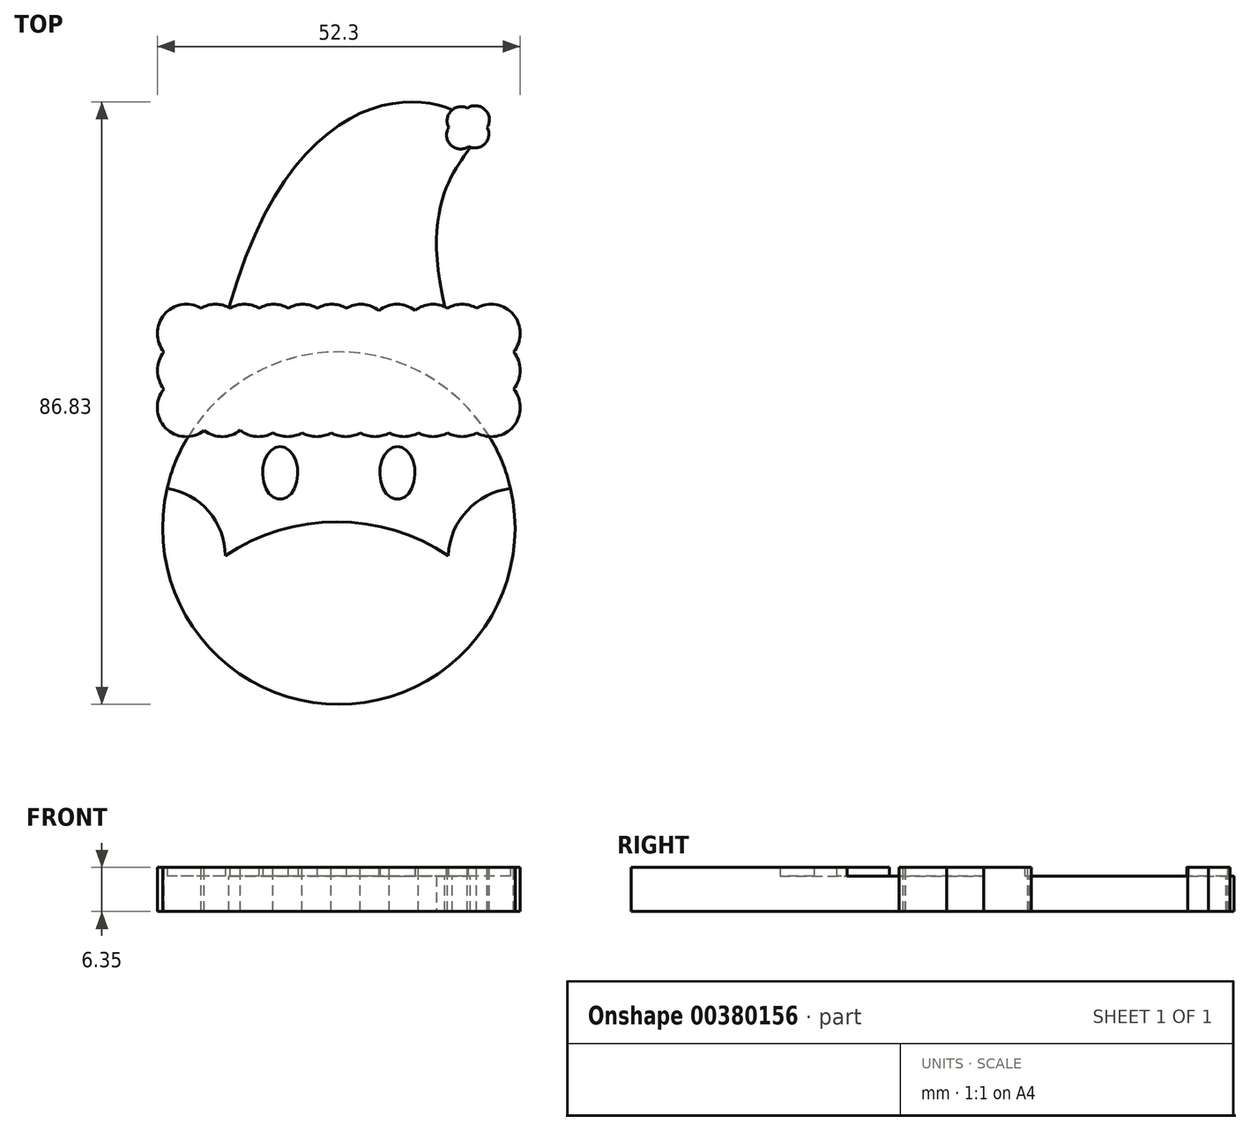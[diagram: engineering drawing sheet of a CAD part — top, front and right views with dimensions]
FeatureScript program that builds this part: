
annotation { "Feature Type Name" : "Feature", "Feature Type Description" : "" }
export const myFeature = defineFeature(function(context is Context, id is Id, definition is map)
    precondition{}
    {
        {
            var Q0;
            Q0=qCreatedBy(makeId("Top.planeOp"),FACE);
            var sketch = newSketch(context, id + "F0", { "sketchPlane" : qUnion([Q0])});
            skCircle(sketch, "E0", {"center": v(0, 0) * mm, "radius": 25.4 * mm});
            skArc(sketch, "E1", {"start": v(-16.36, -3.97) * mm, "mid": v(-18.76, 2.43) * mm, "end": v(-24.75, 5.71) * mm});
            skArc(sketch, "E2", {"start": v(15.78, -3.97) * mm, "mid": v(-0.29, 0.93) * mm, "end": v(-16.36, -3.97) * mm});
            skArc(sketch, "E3", {"start": v(24.75, 5.71) * mm, "mid": v(18.48, 2.52) * mm, "end": v(15.78, -3.97) * mm});
            skSolve(sketch);
        }
        {
            var Q0;
            {var subQ0=sQuery(id+"F0.wireOp",EDGE,"E1");Q0=makeQuery(id+"F0.imprint","IMPRINT",FACE,{"disambiguationData":[TD([[makeQuery(id+"F0.imprint","IMPRINT",EDGE,{"derivedFrom":subQ0}),-1.0]])]});}
            extrude(context, id + "F1", {"entities" : qUnion([Q0]), "depth" : 5.08 * mm});
        }
        {
            var Q0;
            {var subQ0=sQuery(id+"F0.wireOp",EDGE,"E1");Q0=makeQuery(id+"F0.imprint","IMPRINT",FACE,{"disambiguationData":[TD([[makeQuery(id+"F0.imprint","IMPRINT",EDGE,{"derivedFrom":subQ0}),1.0]])]});}
            extrude(context, id + "F2", {"entities" : qUnion([Q0]), "operationType" : NewBodyOperationType.ADD, "depth" : 6.35 * mm});
        }
        {
            var Q0;
            Q0=makeQuery(id+"F1.opExtrude","CAP_FACE",FACE,{"disambiguationData":[OSD([sQuery(id+"F0.wireOp",EDGE,"E0"),sQuery(id+"F0.wireOp",EDGE,"E1"),sQuery(id+"F0.wireOp",EDGE,"E2"),sQuery(id+"F0.wireOp",EDGE,"E3")])],"isStart":false});
            var sketch = newSketch(context, id + "F3", { "sketchPlane" : qUnion([Q0])});
            skLineSegment(sketch, "E4.bottom", {"start": v(21.96, 28.07) * mm, "end": v(-21.96, 28.07) * mm, "construction": true});
            skLineSegment(sketch, "E4.top", {"start": v(21.96, 17.38) * mm, "end": v(-21.96, 17.38) * mm, "construction": true});
            skLineSegment(sketch, "E4.left", {"start": v(21.96, 28.07) * mm, "end": v(21.96, 17.38) * mm, "construction": true});
            skLineSegment(sketch, "E4.right", {"start": v(-21.96, 28.07) * mm, "end": v(-21.96, 17.38) * mm, "construction": true});
            skPoint(sketch, "E4.middle", {"position": v(0, 22.72) * mm});
            skCircle(sketch, "E5", {"center": v(-21.96, 28.07) * mm, "radius": 4.2 * mm});
            skCircle(sketch, "E6", {"center": v(-21.96, 22.72) * mm, "radius": 4.2 * mm});
            skCircle(sketch, "E7", {"center": v(-21.96, 17.38) * mm, "radius": 4.2 * mm});
            skCircle(sketch, "E8", {"center": v(-17.77, 28.07) * mm, "radius": 4.2 * mm});
            skCircle(sketch, "E9", {"center": v(-13.58, 28.07) * mm, "radius": 4.2 * mm});
            skCircle(sketch, "E10", {"center": v(-9.39, 28.07) * mm, "radius": 4.2 * mm});
            skCircle(sketch, "E11", {"center": v(-5.2, 28.07) * mm, "radius": 4.2 * mm});
            skPoint(sketch, "E11.centerSnap0", {"position": v(0, 28.07) * mm});
            skCircle(sketch, "E12", {"center": v(-1, 28.07) * mm, "radius": 4.2 * mm});
            skCircle(sketch, "E13", {"center": v(3.19, 28.07) * mm, "radius": 4.2 * mm});
            skCircle(sketch, "E14", {"center": v(21.96, 28.07) * mm, "radius": 4.2 * mm});
            skCircle(sketch, "E15", {"center": v(17.77, 28.07) * mm, "radius": 4.2 * mm});
            skCircle(sketch, "E16", {"center": v(13.58, 28.07) * mm, "radius": 4.2 * mm});
            skCircle(sketch, "E17", {"center": v(8.4, 28.07) * mm, "radius": 4.2 * mm});
            skCircle(sketch, "E18", {"center": v(21.96, 22.72) * mm, "radius": 4.2 * mm});
            skCircle(sketch, "E19", {"center": v(21.96, 17.38) * mm, "radius": 4.2 * mm});
            skCircle(sketch, "E20", {"center": v(17.77, 17.38) * mm, "radius": 4.2 * mm});
            skCircle(sketch, "E21", {"center": v(13.58, 17.38) * mm, "radius": 4.2 * mm});
            skCircle(sketch, "E22", {"center": v(9.39, 17.38) * mm, "radius": 4.2 * mm});
            skCircle(sketch, "E23", {"center": v(5.2, 17.38) * mm, "radius": 4.2 * mm});
            skCircle(sketch, "E24", {"center": v(1, 17.38) * mm, "radius": 4.2 * mm});
            skCircle(sketch, "E25", {"center": v(-3.19, 17.38) * mm, "radius": 4.2 * mm});
            skCircle(sketch, "E26", {"center": v(-7.38, 17.38) * mm, "radius": 4.2 * mm});
            skCircle(sketch, "E27", {"center": v(-11.57, 17.38) * mm, "radius": 4.2 * mm});
            skCircle(sketch, "E28", {"center": v(-16.84, 17.38) * mm, "radius": 4.2 * mm});
            skSolve(sketch);
        }
        {
            var Q0;
            {var subQ0=sQuery(id+"F3.wireOp",EDGE,"E8");var subQ1=sQuery(id+"F3.wireOp",EDGE,"E5");var subQ2=makeQuery(id+"F3.imprint","INTERSECT",VERTEX,{"disambiguationData":[OD(0.0)],"derivedFrom":[subQ1,subQ0]});Q0=makeQuery(id+"F3.imprint","IMPRINT",FACE,{"disambiguationData":[TD([[makeQuery(id+"F3.imprint","IMPRINT",EDGE,{"disambiguationData":[TD([[subQ2,-1.0]])],"derivedFrom":subQ1}),1.0]])]});}
            var Q1;
            {var subQ0=sQuery(id+"F3.wireOp",EDGE,"E8");var subQ1=sQuery(id+"F3.wireOp",EDGE,"E5");var subQ2=makeQuery(id+"F3.imprint","INTERSECT",VERTEX,{"disambiguationData":[OD(0.0)],"derivedFrom":[subQ1,subQ0]});Q1=makeQuery(id+"F3.imprint","IMPRINT",FACE,{"disambiguationData":[TD([[makeQuery(id+"F3.imprint","IMPRINT",EDGE,{"disambiguationData":[TD([[subQ2,1.0]])],"derivedFrom":subQ1}),1.0]])]});}
            var Q2;
            {var subQ0=sQuery(id+"F3.wireOp",EDGE,"E8");var subQ1=sQuery(id+"F3.wireOp",EDGE,"E5");var subQ2=makeQuery(id+"F3.imprint","INTERSECT",VERTEX,{"disambiguationData":[OD(0.0)],"derivedFrom":[subQ1,subQ0]});Q2=makeQuery(id+"F3.imprint","IMPRINT",FACE,{"disambiguationData":[TD([[makeQuery(id+"F3.imprint","IMPRINT",EDGE,{"disambiguationData":[TD([[subQ2,1.0]])],"derivedFrom":subQ1}),-1.0]])]});}
            var Q3;
            {var subQ0=sQuery(id+"F3.wireOp",EDGE,"E9");var subQ1=sQuery(id+"F3.wireOp",EDGE,"E8");var subQ2=makeQuery(id+"F3.imprint","INTERSECT",VERTEX,{"disambiguationData":[OD(0.0)],"derivedFrom":[subQ1,subQ0]});Q3=makeQuery(id+"F3.imprint","IMPRINT",FACE,{"disambiguationData":[TD([[makeQuery(id+"F3.imprint","IMPRINT",EDGE,{"disambiguationData":[TD([[subQ2,1.0]])],"derivedFrom":subQ1}),1.0]])]});}
            var Q4;
            {var subQ0=sQuery(id+"F3.wireOp",EDGE,"E9");var subQ1=sQuery(id+"F3.wireOp",EDGE,"E5");var subQ2=makeQuery(id+"F3.imprint","INTERSECT",VERTEX,{"derivedFrom":[subQ1,subQ0]});Q4=makeQuery(id+"F3.imprint","IMPRINT",FACE,{"disambiguationData":[TD([[makeQuery(id+"F3.imprint","IMPRINT",EDGE,{"disambiguationData":[TD([[subQ2,1.0]])],"derivedFrom":subQ1}),-1.0]])]});}
            var Q5;
            {var subQ5=sQuery(id+"F3.wireOp",EDGE,"E8");var subQ7=sQuery(id+"F3.wireOp",EDGE,"E6");var subQ8=makeQuery(id+"F3.imprint","INTERSECT",VERTEX,{"disambiguationData":[OD(0.0)],"derivedFrom":[subQ7,subQ5]});Q5=makeQuery(id+"F3.imprint","IMPRINT",FACE,{"disambiguationData":[TD([[makeQuery(id+"F3.imprint","IMPRINT",EDGE,{"disambiguationData":[TD([[subQ8,1.0]])],"derivedFrom":subQ7}),-1.0]])]});}
            var Q6;
            {var subQ1=sQuery(id+"F3.wireOp",EDGE,"E15");var subQ5=sQuery(id+"F3.wireOp",EDGE,"E16");var subQ6=makeQuery(id+"F3.imprint","INTERSECT",VERTEX,{"disambiguationData":[OD(1.0)],"derivedFrom":[subQ1,subQ5]});Q6=makeQuery(id+"F3.imprint","IMPRINT",FACE,{"disambiguationData":[TD([[makeQuery(id+"F3.imprint","IMPRINT",EDGE,{"disambiguationData":[TD([[subQ6,-1.0]])],"derivedFrom":subQ1}),-1.0]])]});}
            var Q7;
            {var subQ0=sQuery(id+"F3.wireOp",EDGE,"E10");var subQ1=sQuery(id+"F3.wireOp",EDGE,"E8");var subQ2=makeQuery(id+"F3.imprint","INTERSECT",VERTEX,{"derivedFrom":[subQ1,subQ0]});Q7=makeQuery(id+"F3.imprint","IMPRINT",FACE,{"disambiguationData":[TD([[makeQuery(id+"F3.imprint","IMPRINT",EDGE,{"disambiguationData":[TD([[subQ2,1.0]])],"derivedFrom":subQ1}),-1.0]])]});}
            var Q8;
            {var subQ0=sQuery(id+"F3.wireOp",EDGE,"E9");var subQ1=sQuery(id+"F3.wireOp",EDGE,"E8");var subQ2=makeQuery(id+"F3.imprint","INTERSECT",VERTEX,{"disambiguationData":[OD(0.0)],"derivedFrom":[subQ1,subQ0]});Q8=makeQuery(id+"F3.imprint","IMPRINT",FACE,{"disambiguationData":[TD([[makeQuery(id+"F3.imprint","IMPRINT",EDGE,{"disambiguationData":[TD([[subQ2,1.0]])],"derivedFrom":subQ1}),-1.0]])]});}
            var Q9;
            {var subQ0=sQuery(id+"F3.wireOp",EDGE,"E10");var subQ1=sQuery(id+"F3.wireOp",EDGE,"E9");var subQ2=makeQuery(id+"F3.imprint","INTERSECT",VERTEX,{"disambiguationData":[OD(0.0)],"derivedFrom":[subQ1,subQ0]});Q9=makeQuery(id+"F3.imprint","IMPRINT",FACE,{"disambiguationData":[TD([[makeQuery(id+"F3.imprint","IMPRINT",EDGE,{"disambiguationData":[TD([[subQ2,1.0]])],"derivedFrom":subQ1}),1.0]])]});}
            var Q10;
            {var subQ0=sQuery(id+"F3.wireOp",EDGE,"E10");var subQ1=sQuery(id+"F3.wireOp",EDGE,"E9");var subQ2=makeQuery(id+"F3.imprint","INTERSECT",VERTEX,{"disambiguationData":[OD(0.0)],"derivedFrom":[subQ1,subQ0]});Q10=makeQuery(id+"F3.imprint","IMPRINT",FACE,{"disambiguationData":[TD([[makeQuery(id+"F3.imprint","IMPRINT",EDGE,{"disambiguationData":[TD([[subQ2,1.0]])],"derivedFrom":subQ1}),-1.0]])]});}
            var Q11;
            {var subQ0=sQuery(id+"F3.wireOp",EDGE,"E11");var subQ1=sQuery(id+"F3.wireOp",EDGE,"E10");var subQ2=makeQuery(id+"F3.imprint","INTERSECT",VERTEX,{"disambiguationData":[OD(0.0)],"derivedFrom":[subQ1,subQ0]});Q11=makeQuery(id+"F3.imprint","IMPRINT",FACE,{"disambiguationData":[TD([[makeQuery(id+"F3.imprint","IMPRINT",EDGE,{"disambiguationData":[TD([[subQ2,1.0]])],"derivedFrom":subQ1}),1.0]])]});}
            var Q12;
            {var subQ0=sQuery(id+"F3.wireOp",EDGE,"E11");var subQ1=sQuery(id+"F3.wireOp",EDGE,"E10");var subQ2=makeQuery(id+"F3.imprint","INTERSECT",VERTEX,{"disambiguationData":[OD(0.0)],"derivedFrom":[subQ1,subQ0]});Q12=makeQuery(id+"F3.imprint","IMPRINT",FACE,{"disambiguationData":[TD([[makeQuery(id+"F3.imprint","IMPRINT",EDGE,{"disambiguationData":[TD([[subQ2,1.0]])],"derivedFrom":subQ1}),1.0]])]});}
            var Q13;
            {var subQ0=sQuery(id+"F3.wireOp",EDGE,"E11");var subQ1=sQuery(id+"F3.wireOp",EDGE,"E9");var subQ2=makeQuery(id+"F3.imprint","INTERSECT",VERTEX,{"derivedFrom":[subQ1,subQ0]});Q13=makeQuery(id+"F3.imprint","IMPRINT",FACE,{"disambiguationData":[TD([[makeQuery(id+"F3.imprint","IMPRINT",EDGE,{"disambiguationData":[TD([[subQ2,1.0]])],"derivedFrom":subQ1}),-1.0]])]});}
            var Q14;
            {var subQ0=sQuery(id+"F3.wireOp",EDGE,"E12");var subQ1=sQuery(id+"F3.wireOp",EDGE,"E10");var subQ2=makeQuery(id+"F3.imprint","INTERSECT",VERTEX,{"derivedFrom":[subQ1,subQ0]});Q14=makeQuery(id+"F3.imprint","IMPRINT",FACE,{"disambiguationData":[TD([[makeQuery(id+"F3.imprint","IMPRINT",EDGE,{"disambiguationData":[TD([[subQ2,1.0]])],"derivedFrom":subQ1}),-1.0]])]});}
            var Q15;
            {var subQ0=sQuery(id+"F3.wireOp",EDGE,"E12");var subQ1=sQuery(id+"F3.wireOp",EDGE,"E11");var subQ2=makeQuery(id+"F3.imprint","INTERSECT",VERTEX,{"disambiguationData":[OD(0.0)],"derivedFrom":[subQ1,subQ0]});Q15=makeQuery(id+"F3.imprint","IMPRINT",FACE,{"disambiguationData":[TD([[makeQuery(id+"F3.imprint","IMPRINT",EDGE,{"disambiguationData":[TD([[subQ2,1.0]])],"derivedFrom":subQ1}),1.0]])]});}
            var Q16;
            {var subQ0=sQuery(id+"F3.wireOp",EDGE,"E11");var subQ1=sQuery(id+"F3.wireOp",EDGE,"E10");var subQ2=makeQuery(id+"F3.imprint","INTERSECT",VERTEX,{"disambiguationData":[OD(0.0)],"derivedFrom":[subQ1,subQ0]});Q16=makeQuery(id+"F3.imprint","IMPRINT",FACE,{"disambiguationData":[TD([[makeQuery(id+"F3.imprint","IMPRINT",EDGE,{"disambiguationData":[TD([[subQ2,1.0]])],"derivedFrom":subQ1}),-1.0]])]});}
            var Q17;
            {var subQ0=sQuery(id+"F3.wireOp",EDGE,"E13");var subQ1=sQuery(id+"F3.wireOp",EDGE,"E11");var subQ2=makeQuery(id+"F3.imprint","INTERSECT",VERTEX,{"derivedFrom":[subQ1,subQ0]});Q17=makeQuery(id+"F3.imprint","IMPRINT",FACE,{"disambiguationData":[TD([[makeQuery(id+"F3.imprint","IMPRINT",EDGE,{"disambiguationData":[TD([[subQ2,1.0]])],"derivedFrom":subQ1}),-1.0]])]});}
            var Q18;
            {var subQ0=sQuery(id+"F3.wireOp",EDGE,"E13");var subQ1=sQuery(id+"F3.wireOp",EDGE,"E12");var subQ2=makeQuery(id+"F3.imprint","INTERSECT",VERTEX,{"disambiguationData":[OD(0.0)],"derivedFrom":[subQ1,subQ0]});Q18=makeQuery(id+"F3.imprint","IMPRINT",FACE,{"disambiguationData":[TD([[makeQuery(id+"F3.imprint","IMPRINT",EDGE,{"disambiguationData":[TD([[subQ2,1.0]])],"derivedFrom":subQ1}),1.0]])]});}
            var Q19;
            {var subQ0=sQuery(id+"F3.wireOp",EDGE,"E12");var subQ1=sQuery(id+"F3.wireOp",EDGE,"E11");var subQ2=makeQuery(id+"F3.imprint","INTERSECT",VERTEX,{"disambiguationData":[OD(0.0)],"derivedFrom":[subQ1,subQ0]});Q19=makeQuery(id+"F3.imprint","IMPRINT",FACE,{"disambiguationData":[TD([[makeQuery(id+"F3.imprint","IMPRINT",EDGE,{"disambiguationData":[TD([[subQ2,1.0]])],"derivedFrom":subQ1}),-1.0]])]});}
            var Q20;
            {var subQ1=sQuery(id+"F3.wireOp",EDGE,"E13");var subQ5=sQuery(id+"F3.wireOp",EDGE,"E12");var subQ6=makeQuery(id+"F3.imprint","INTERSECT",VERTEX,{"disambiguationData":[OD(0.0)],"derivedFrom":[subQ5,subQ1]});Q20=makeQuery(id+"F3.imprint","IMPRINT",FACE,{"disambiguationData":[TD([[makeQuery(id+"F3.imprint","IMPRINT",EDGE,{"disambiguationData":[TD([[subQ6,1.0]])],"derivedFrom":subQ5}),-1.0]])]});}
            var Q21;
            {var subQ0=sQuery(id+"F3.wireOp",EDGE,"E17");var subQ1=sQuery(id+"F3.wireOp",EDGE,"E13");var subQ2=makeQuery(id+"F3.imprint","INTERSECT",VERTEX,{"disambiguationData":[OD(0.0)],"derivedFrom":[subQ1,subQ0]});Q21=makeQuery(id+"F3.imprint","IMPRINT",FACE,{"disambiguationData":[TD([[makeQuery(id+"F3.imprint","IMPRINT",EDGE,{"disambiguationData":[TD([[subQ2,1.0]])],"derivedFrom":subQ1}),1.0]])]});}
            var Q22;
            {var subQ0=sQuery(id+"F3.wireOp",EDGE,"E17");var subQ1=sQuery(id+"F3.wireOp",EDGE,"E13");var subQ2=makeQuery(id+"F3.imprint","INTERSECT",VERTEX,{"disambiguationData":[OD(0.0)],"derivedFrom":[subQ1,subQ0]});Q22=makeQuery(id+"F3.imprint","IMPRINT",FACE,{"disambiguationData":[TD([[makeQuery(id+"F3.imprint","IMPRINT",EDGE,{"disambiguationData":[TD([[subQ2,1.0]])],"derivedFrom":subQ1}),-1.0]])]});}
            var Q23;
            {var subQ0=sQuery(id+"F3.wireOp",EDGE,"E17");var subQ1=sQuery(id+"F3.wireOp",EDGE,"E16");var subQ2=makeQuery(id+"F3.imprint","INTERSECT",VERTEX,{"disambiguationData":[OD(0.0)],"derivedFrom":[subQ1,subQ0]});Q23=makeQuery(id+"F3.imprint","IMPRINT",FACE,{"disambiguationData":[TD([[makeQuery(id+"F3.imprint","IMPRINT",EDGE,{"disambiguationData":[TD([[subQ2,-1.0]])],"derivedFrom":subQ1}),1.0]])]});}
            var Q24;
            {var subQ0=sQuery(id+"F3.wireOp",EDGE,"E16");var subQ1=sQuery(id+"F3.wireOp",EDGE,"E15");var subQ2=makeQuery(id+"F3.imprint","INTERSECT",VERTEX,{"disambiguationData":[OD(0.0)],"derivedFrom":[subQ1,subQ0]});Q24=makeQuery(id+"F3.imprint","IMPRINT",FACE,{"disambiguationData":[TD([[makeQuery(id+"F3.imprint","IMPRINT",EDGE,{"disambiguationData":[TD([[subQ2,-1.0]])],"derivedFrom":subQ1}),-1.0]])]});}
            var Q25;
            {var subQ0=sQuery(id+"F3.wireOp",EDGE,"E16");var subQ1=sQuery(id+"F3.wireOp",EDGE,"E15");var subQ2=makeQuery(id+"F3.imprint","INTERSECT",VERTEX,{"disambiguationData":[OD(0.0)],"derivedFrom":[subQ1,subQ0]});Q25=makeQuery(id+"F3.imprint","IMPRINT",FACE,{"disambiguationData":[TD([[makeQuery(id+"F3.imprint","IMPRINT",EDGE,{"disambiguationData":[TD([[subQ2,-1.0]])],"derivedFrom":subQ1}),1.0]])]});}
            var Q26;
            {var subQ0=sQuery(id+"F3.wireOp",EDGE,"E15");var subQ1=sQuery(id+"F3.wireOp",EDGE,"E14");var subQ2=makeQuery(id+"F3.imprint","INTERSECT",VERTEX,{"disambiguationData":[OD(0.0)],"derivedFrom":[subQ1,subQ0]});Q26=makeQuery(id+"F3.imprint","IMPRINT",FACE,{"disambiguationData":[TD([[makeQuery(id+"F3.imprint","IMPRINT",EDGE,{"disambiguationData":[TD([[subQ2,-1.0]])],"derivedFrom":subQ1}),-1.0]])]});}
            var Q27;
            {var subQ0=sQuery(id+"F3.wireOp",EDGE,"E16");var subQ1=sQuery(id+"F3.wireOp",EDGE,"E14");var subQ2=makeQuery(id+"F3.imprint","INTERSECT",VERTEX,{"derivedFrom":[subQ1,subQ0]});Q27=makeQuery(id+"F3.imprint","IMPRINT",FACE,{"disambiguationData":[TD([[makeQuery(id+"F3.imprint","IMPRINT",EDGE,{"disambiguationData":[TD([[subQ2,-1.0]])],"derivedFrom":subQ1}),-1.0]])]});}
            var Q28;
            {var subQ0=sQuery(id+"F3.wireOp",EDGE,"E18");var subQ1=sQuery(id+"F3.wireOp",EDGE,"E14");var subQ2=makeQuery(id+"F3.imprint","INTERSECT",VERTEX,{"disambiguationData":[OD(1.0)],"derivedFrom":[subQ1,subQ0]});Q28=makeQuery(id+"F3.imprint","IMPRINT",FACE,{"disambiguationData":[TD([[makeQuery(id+"F3.imprint","IMPRINT",EDGE,{"disambiguationData":[TD([[subQ2,-1.0]])],"derivedFrom":subQ1}),-1.0]])]});}
            var Q29;
            {var subQ0=sQuery(id+"F3.wireOp",EDGE,"E18");var subQ1=sQuery(id+"F3.wireOp",EDGE,"E14");var subQ2=makeQuery(id+"F3.imprint","INTERSECT",VERTEX,{"disambiguationData":[OD(1.0)],"derivedFrom":[subQ1,subQ0]});Q29=makeQuery(id+"F3.imprint","IMPRINT",FACE,{"disambiguationData":[TD([[makeQuery(id+"F3.imprint","IMPRINT",EDGE,{"disambiguationData":[TD([[subQ2,-1.0]])],"derivedFrom":subQ1}),1.0]])]});}
            var Q30;
            {var subQ0=sQuery(id+"F3.wireOp",EDGE,"E15");var subQ1=sQuery(id+"F3.wireOp",EDGE,"E14");var subQ2=makeQuery(id+"F3.imprint","INTERSECT",VERTEX,{"disambiguationData":[OD(0.0)],"derivedFrom":[subQ1,subQ0]});Q30=makeQuery(id+"F3.imprint","IMPRINT",FACE,{"disambiguationData":[TD([[makeQuery(id+"F3.imprint","IMPRINT",EDGE,{"disambiguationData":[TD([[subQ2,-1.0]])],"derivedFrom":subQ1}),1.0]])]});}
            var Q31;
            {var subQ0=sQuery(id+"F3.wireOp",EDGE,"E15");var subQ1=sQuery(id+"F3.wireOp",EDGE,"E14");var subQ2=makeQuery(id+"F3.imprint","INTERSECT",VERTEX,{"disambiguationData":[OD(0.0)],"derivedFrom":[subQ1,subQ0]});Q31=makeQuery(id+"F3.imprint","IMPRINT",FACE,{"disambiguationData":[TD([[makeQuery(id+"F3.imprint","IMPRINT",EDGE,{"disambiguationData":[TD([[subQ2,1.0]])],"derivedFrom":subQ1}),1.0]])]});}
            var Q32;
            {var subQ0=sQuery(id+"F3.wireOp",EDGE,"E18");var subQ1=sQuery(id+"F3.wireOp",EDGE,"E14");var subQ2=makeQuery(id+"F3.imprint","INTERSECT",VERTEX,{"disambiguationData":[OD(0.0)],"derivedFrom":[subQ1,subQ0]});Q32=makeQuery(id+"F3.imprint","IMPRINT",FACE,{"disambiguationData":[TD([[makeQuery(id+"F3.imprint","IMPRINT",EDGE,{"disambiguationData":[TD([[subQ2,1.0]])],"derivedFrom":subQ1}),1.0]])]});}
            var Q33;
            {var subQ0=sQuery(id+"F3.wireOp",EDGE,"E18");var subQ1=sQuery(id+"F3.wireOp",EDGE,"E14");var subQ2=makeQuery(id+"F3.imprint","INTERSECT",VERTEX,{"disambiguationData":[OD(0.0)],"derivedFrom":[subQ1,subQ0]});Q33=makeQuery(id+"F3.imprint","IMPRINT",FACE,{"disambiguationData":[TD([[makeQuery(id+"F3.imprint","IMPRINT",EDGE,{"disambiguationData":[TD([[subQ2,1.0]])],"derivedFrom":subQ1}),-1.0]])]});}
            var Q34;
            {var subQ0=sQuery(id+"F3.wireOp",EDGE,"E19");var subQ1=sQuery(id+"F3.wireOp",EDGE,"E18");var subQ2=makeQuery(id+"F3.imprint","INTERSECT",VERTEX,{"disambiguationData":[OD(0.0)],"derivedFrom":[subQ1,subQ0]});Q34=makeQuery(id+"F3.imprint","IMPRINT",FACE,{"disambiguationData":[TD([[makeQuery(id+"F3.imprint","IMPRINT",EDGE,{"disambiguationData":[TD([[subQ2,1.0]])],"derivedFrom":subQ1}),1.0]])]});}
            var Q35;
            {var subQ0=sQuery(id+"F3.wireOp",EDGE,"E19");var subQ1=sQuery(id+"F3.wireOp",EDGE,"E18");var subQ2=makeQuery(id+"F3.imprint","INTERSECT",VERTEX,{"disambiguationData":[OD(0.0)],"derivedFrom":[subQ1,subQ0]});Q35=makeQuery(id+"F3.imprint","IMPRINT",FACE,{"disambiguationData":[TD([[makeQuery(id+"F3.imprint","IMPRINT",EDGE,{"disambiguationData":[TD([[subQ2,1.0]])],"derivedFrom":subQ1}),-1.0]])]});}
            var Q36;
            {var subQ0=sQuery(id+"F3.wireOp",EDGE,"E19");var subQ1=sQuery(id+"F3.wireOp",EDGE,"E18");var subQ2=makeQuery(id+"F3.imprint","INTERSECT",VERTEX,{"disambiguationData":[OD(1.0)],"derivedFrom":[subQ1,subQ0]});Q36=makeQuery(id+"F3.imprint","IMPRINT",FACE,{"disambiguationData":[TD([[makeQuery(id+"F3.imprint","IMPRINT",EDGE,{"disambiguationData":[TD([[subQ2,-1.0]])],"derivedFrom":subQ1}),-1.0]])]});}
            var Q37;
            {var subQ0=sQuery(id+"F3.wireOp",EDGE,"E20");var subQ1=sQuery(id+"F3.wireOp",EDGE,"E18");var subQ2=makeQuery(id+"F3.imprint","INTERSECT",VERTEX,{"disambiguationData":[OD(0.0)],"derivedFrom":[subQ1,subQ0]});Q37=makeQuery(id+"F3.imprint","IMPRINT",FACE,{"disambiguationData":[TD([[makeQuery(id+"F3.imprint","IMPRINT",EDGE,{"disambiguationData":[TD([[subQ2,-1.0]])],"derivedFrom":subQ1}),1.0]])]});}
            var Q38;
            {var subQ0=sQuery(id+"F3.wireOp",EDGE,"E20");var subQ1=sQuery(id+"F3.wireOp",EDGE,"E18");var subQ2=makeQuery(id+"F3.imprint","INTERSECT",VERTEX,{"disambiguationData":[OD(0.0)],"derivedFrom":[subQ1,subQ0]});Q38=makeQuery(id+"F3.imprint","IMPRINT",FACE,{"disambiguationData":[TD([[makeQuery(id+"F3.imprint","IMPRINT",EDGE,{"disambiguationData":[TD([[subQ2,-1.0]])],"derivedFrom":subQ1}),-1.0]])]});}
            var Q39;
            {var subQ0=sQuery(id+"F3.wireOp",EDGE,"E21");var subQ1=sQuery(id+"F3.wireOp",EDGE,"E19");var subQ2=makeQuery(id+"F3.imprint","INTERSECT",VERTEX,{"derivedFrom":[subQ1,subQ0]});Q39=makeQuery(id+"F3.imprint","IMPRINT",FACE,{"disambiguationData":[TD([[makeQuery(id+"F3.imprint","IMPRINT",EDGE,{"disambiguationData":[TD([[subQ2,-1.0]])],"derivedFrom":subQ1}),-1.0]])]});}
            var Q40;
            {var subQ2=sQuery(id+"F3.wireOp",EDGE,"E20");var subQ4=makeQuery(id+"F3.imprint","INTERSECT",VERTEX,{"derivedFrom":[subQ2,sQuery(id+"F3.wireOp",EDGE,"E22")]});Q40=makeQuery(id+"F3.imprint","IMPRINT",FACE,{"disambiguationData":[TD([[makeQuery(id+"F3.imprint","IMPRINT",EDGE,{"disambiguationData":[TD([[subQ4,1.0]])],"derivedFrom":subQ2}),1.0]])]});}
            var Q41;
            {var subQ0=sQuery(id+"F3.wireOp",EDGE,"E19");var subQ1=sQuery(id+"F3.wireOp",EDGE,"E18");var subQ2=makeQuery(id+"F3.imprint","INTERSECT",VERTEX,{"disambiguationData":[OD(1.0)],"derivedFrom":[subQ1,subQ0]});Q41=makeQuery(id+"F3.imprint","IMPRINT",FACE,{"disambiguationData":[TD([[makeQuery(id+"F3.imprint","IMPRINT",EDGE,{"disambiguationData":[TD([[subQ2,-1.0]])],"derivedFrom":subQ1}),1.0]])]});}
            var Q42;
            {var subQ0=sQuery(id+"F3.wireOp",EDGE,"E21");var subQ1=sQuery(id+"F3.wireOp",EDGE,"E20");var subQ2=makeQuery(id+"F3.imprint","INTERSECT",VERTEX,{"disambiguationData":[OD(0.0)],"derivedFrom":[subQ1,subQ0]});Q42=makeQuery(id+"F3.imprint","IMPRINT",FACE,{"disambiguationData":[TD([[makeQuery(id+"F3.imprint","IMPRINT",EDGE,{"disambiguationData":[TD([[subQ2,-1.0]])],"derivedFrom":subQ1}),1.0]])]});}
            var Q43;
            {var subQ0=sQuery(id+"F3.wireOp",EDGE,"E21");var subQ1=sQuery(id+"F3.wireOp",EDGE,"E20");var subQ2=makeQuery(id+"F3.imprint","INTERSECT",VERTEX,{"disambiguationData":[OD(0.0)],"derivedFrom":[subQ1,subQ0]});Q43=makeQuery(id+"F3.imprint","IMPRINT",FACE,{"disambiguationData":[TD([[makeQuery(id+"F3.imprint","IMPRINT",EDGE,{"disambiguationData":[TD([[subQ2,-1.0]])],"derivedFrom":subQ1}),-1.0]])]});}
            var Q44;
            {var subQ0=sQuery(id+"F3.wireOp",EDGE,"E22");var subQ1=sQuery(id+"F3.wireOp",EDGE,"E21");var subQ2=makeQuery(id+"F3.imprint","INTERSECT",VERTEX,{"disambiguationData":[OD(0.0)],"derivedFrom":[subQ1,subQ0]});Q44=makeQuery(id+"F3.imprint","IMPRINT",FACE,{"disambiguationData":[TD([[makeQuery(id+"F3.imprint","IMPRINT",EDGE,{"disambiguationData":[TD([[subQ2,-1.0]])],"derivedFrom":subQ1}),1.0]])]});}
            var Q45;
            {var subQ0=sQuery(id+"F3.wireOp",EDGE,"E22");var subQ1=sQuery(id+"F3.wireOp",EDGE,"E20");var subQ2=makeQuery(id+"F3.imprint","INTERSECT",VERTEX,{"derivedFrom":[subQ1,subQ0]});Q45=makeQuery(id+"F3.imprint","IMPRINT",FACE,{"disambiguationData":[TD([[makeQuery(id+"F3.imprint","IMPRINT",EDGE,{"disambiguationData":[TD([[subQ2,-1.0]])],"derivedFrom":subQ1}),-1.0]])]});}
            var Q46;
            {var subQ0=sQuery(id+"F3.wireOp",EDGE,"E19");var subQ1=makeQuery(id+"F3.imprint","INTERSECT",VERTEX,{"derivedFrom":[subQ0,sQuery(id+"F3.wireOp",EDGE,"E21")]});Q46=makeQuery(id+"F3.imprint","IMPRINT",FACE,{"disambiguationData":[TD([[makeQuery(id+"F3.imprint","IMPRINT",EDGE,{"disambiguationData":[TD([[subQ1,1.0]])],"derivedFrom":subQ0}),1.0]])]});}
            var Q47;
            {var subQ0=sQuery(id+"F3.wireOp",EDGE,"E20");var subQ1=sQuery(id+"F3.wireOp",EDGE,"E19");var subQ2=makeQuery(id+"F3.imprint","INTERSECT",VERTEX,{"disambiguationData":[OD(1.0)],"derivedFrom":[subQ1,subQ0]});Q47=makeQuery(id+"F3.imprint","IMPRINT",FACE,{"disambiguationData":[TD([[makeQuery(id+"F3.imprint","IMPRINT",EDGE,{"disambiguationData":[TD([[subQ2,-1.0]])],"derivedFrom":subQ1}),1.0]])]});}
            var Q48;
            {var subQ0=sQuery(id+"F3.wireOp",EDGE,"E22");var subQ1=sQuery(id+"F3.wireOp",EDGE,"E20");var subQ2=makeQuery(id+"F3.imprint","INTERSECT",VERTEX,{"derivedFrom":[subQ1,subQ0]});Q48=makeQuery(id+"F3.imprint","IMPRINT",FACE,{"disambiguationData":[TD([[makeQuery(id+"F3.imprint","IMPRINT",EDGE,{"disambiguationData":[TD([[subQ2,1.0]])],"derivedFrom":subQ1}),-1.0]])]});}
            var Q49;
            {var subQ0=sQuery(id+"F3.wireOp",EDGE,"E22");var subQ1=sQuery(id+"F3.wireOp",EDGE,"E21");var subQ2=makeQuery(id+"F3.imprint","INTERSECT",VERTEX,{"disambiguationData":[OD(0.0)],"derivedFrom":[subQ1,subQ0]});Q49=makeQuery(id+"F3.imprint","IMPRINT",FACE,{"disambiguationData":[TD([[makeQuery(id+"F3.imprint","IMPRINT",EDGE,{"disambiguationData":[TD([[subQ2,-1.0]])],"derivedFrom":subQ1}),-1.0]])]});}
            var Q50;
            {var subQ0=sQuery(id+"F3.wireOp",EDGE,"E23");var subQ1=sQuery(id+"F3.wireOp",EDGE,"E21");var subQ2=makeQuery(id+"F3.imprint","INTERSECT",VERTEX,{"derivedFrom":[subQ1,subQ0]});Q50=makeQuery(id+"F3.imprint","IMPRINT",FACE,{"disambiguationData":[TD([[makeQuery(id+"F3.imprint","IMPRINT",EDGE,{"disambiguationData":[TD([[subQ2,-1.0]])],"derivedFrom":subQ1}),-1.0]])]});}
            var Q51;
            {var subQ0=sQuery(id+"F3.wireOp",EDGE,"E23");var subQ1=sQuery(id+"F3.wireOp",EDGE,"E22");var subQ2=makeQuery(id+"F3.imprint","INTERSECT",VERTEX,{"disambiguationData":[OD(0.0)],"derivedFrom":[subQ1,subQ0]});Q51=makeQuery(id+"F3.imprint","IMPRINT",FACE,{"disambiguationData":[TD([[makeQuery(id+"F3.imprint","IMPRINT",EDGE,{"disambiguationData":[TD([[subQ2,-1.0]])],"derivedFrom":subQ1}),1.0]])]});}
            var Q52;
            {var subQ0=sQuery(id+"F3.wireOp",EDGE,"E23");var subQ1=sQuery(id+"F3.wireOp",EDGE,"E22");var subQ2=makeQuery(id+"F3.imprint","INTERSECT",VERTEX,{"disambiguationData":[OD(0.0)],"derivedFrom":[subQ1,subQ0]});Q52=makeQuery(id+"F3.imprint","IMPRINT",FACE,{"disambiguationData":[TD([[makeQuery(id+"F3.imprint","IMPRINT",EDGE,{"disambiguationData":[TD([[subQ2,-1.0]])],"derivedFrom":subQ1}),-1.0]])]});}
            var Q53;
            {var subQ0=sQuery(id+"F3.wireOp",EDGE,"E24");var subQ1=sQuery(id+"F3.wireOp",EDGE,"E22");var subQ2=makeQuery(id+"F3.imprint","INTERSECT",VERTEX,{"derivedFrom":[subQ1,subQ0]});Q53=makeQuery(id+"F3.imprint","IMPRINT",FACE,{"disambiguationData":[TD([[makeQuery(id+"F3.imprint","IMPRINT",EDGE,{"disambiguationData":[TD([[subQ2,-1.0]])],"derivedFrom":subQ1}),-1.0]])]});}
            var Q54;
            {var subQ0=sQuery(id+"F3.wireOp",EDGE,"E24");var subQ1=sQuery(id+"F3.wireOp",EDGE,"E23");var subQ2=makeQuery(id+"F3.imprint","INTERSECT",VERTEX,{"disambiguationData":[OD(0.0)],"derivedFrom":[subQ1,subQ0]});Q54=makeQuery(id+"F3.imprint","IMPRINT",FACE,{"disambiguationData":[TD([[makeQuery(id+"F3.imprint","IMPRINT",EDGE,{"disambiguationData":[TD([[subQ2,-1.0]])],"derivedFrom":subQ1}),1.0]])]});}
            var Q55;
            {var subQ0=sQuery(id+"F3.wireOp",EDGE,"E24");var subQ1=sQuery(id+"F3.wireOp",EDGE,"E23");var subQ2=makeQuery(id+"F3.imprint","INTERSECT",VERTEX,{"disambiguationData":[OD(0.0)],"derivedFrom":[subQ1,subQ0]});Q55=makeQuery(id+"F3.imprint","IMPRINT",FACE,{"disambiguationData":[TD([[makeQuery(id+"F3.imprint","IMPRINT",EDGE,{"disambiguationData":[TD([[subQ2,-1.0]])],"derivedFrom":subQ1}),-1.0]])]});}
            var Q56;
            {var subQ0=sQuery(id+"F3.wireOp",EDGE,"E25");var subQ1=sQuery(id+"F3.wireOp",EDGE,"E23");var subQ2=makeQuery(id+"F3.imprint","INTERSECT",VERTEX,{"derivedFrom":[subQ1,subQ0]});Q56=makeQuery(id+"F3.imprint","IMPRINT",FACE,{"disambiguationData":[TD([[makeQuery(id+"F3.imprint","IMPRINT",EDGE,{"disambiguationData":[TD([[subQ2,-1.0]])],"derivedFrom":subQ1}),-1.0]])]});}
            var Q57;
            {var subQ0=sQuery(id+"F3.wireOp",EDGE,"E25");var subQ1=sQuery(id+"F3.wireOp",EDGE,"E24");var subQ2=makeQuery(id+"F3.imprint","INTERSECT",VERTEX,{"disambiguationData":[OD(0.0)],"derivedFrom":[subQ1,subQ0]});Q57=makeQuery(id+"F3.imprint","IMPRINT",FACE,{"disambiguationData":[TD([[makeQuery(id+"F3.imprint","IMPRINT",EDGE,{"disambiguationData":[TD([[subQ2,-1.0]])],"derivedFrom":subQ1}),1.0]])]});}
            var Q58;
            {var subQ0=sQuery(id+"F3.wireOp",EDGE,"E25");var subQ1=sQuery(id+"F3.wireOp",EDGE,"E24");var subQ2=makeQuery(id+"F3.imprint","INTERSECT",VERTEX,{"disambiguationData":[OD(0.0)],"derivedFrom":[subQ1,subQ0]});Q58=makeQuery(id+"F3.imprint","IMPRINT",FACE,{"disambiguationData":[TD([[makeQuery(id+"F3.imprint","IMPRINT",EDGE,{"disambiguationData":[TD([[subQ2,-1.0]])],"derivedFrom":subQ1}),-1.0]])]});}
            var Q59;
            {var subQ0=sQuery(id+"F3.wireOp",EDGE,"E26");var subQ1=sQuery(id+"F3.wireOp",EDGE,"E25");var subQ2=makeQuery(id+"F3.imprint","INTERSECT",VERTEX,{"disambiguationData":[OD(0.0)],"derivedFrom":[subQ1,subQ0]});Q59=makeQuery(id+"F3.imprint","IMPRINT",FACE,{"disambiguationData":[TD([[makeQuery(id+"F3.imprint","IMPRINT",EDGE,{"disambiguationData":[TD([[subQ2,-1.0]])],"derivedFrom":subQ1}),1.0]])]});}
            var Q60;
            {var subQ0=sQuery(id+"F3.wireOp",EDGE,"E27");var subQ1=sQuery(id+"F3.wireOp",EDGE,"E25");var subQ2=makeQuery(id+"F3.imprint","INTERSECT",VERTEX,{"derivedFrom":[subQ1,subQ0]});Q60=makeQuery(id+"F3.imprint","IMPRINT",FACE,{"disambiguationData":[TD([[makeQuery(id+"F3.imprint","IMPRINT",EDGE,{"disambiguationData":[TD([[subQ2,-1.0]])],"derivedFrom":subQ1}),-1.0]])]});}
            var Q61;
            {var subQ0=sQuery(id+"F3.wireOp",EDGE,"E26");var subQ1=sQuery(id+"F3.wireOp",EDGE,"E25");var subQ2=makeQuery(id+"F3.imprint","INTERSECT",VERTEX,{"disambiguationData":[OD(0.0)],"derivedFrom":[subQ1,subQ0]});Q61=makeQuery(id+"F3.imprint","IMPRINT",FACE,{"disambiguationData":[TD([[makeQuery(id+"F3.imprint","IMPRINT",EDGE,{"disambiguationData":[TD([[subQ2,-1.0]])],"derivedFrom":subQ1}),-1.0]])]});}
            var Q62;
            {var subQ0=sQuery(id+"F3.wireOp",EDGE,"E27");var subQ1=sQuery(id+"F3.wireOp",EDGE,"E26");var subQ2=makeQuery(id+"F3.imprint","INTERSECT",VERTEX,{"disambiguationData":[OD(0.0)],"derivedFrom":[subQ1,subQ0]});Q62=makeQuery(id+"F3.imprint","IMPRINT",FACE,{"disambiguationData":[TD([[makeQuery(id+"F3.imprint","IMPRINT",EDGE,{"disambiguationData":[TD([[subQ2,-1.0]])],"derivedFrom":subQ1}),1.0]])]});}
            var Q63;
            {var subQ0=sQuery(id+"F3.wireOp",EDGE,"E27");var subQ1=sQuery(id+"F3.wireOp",EDGE,"E26");var subQ2=makeQuery(id+"F3.imprint","INTERSECT",VERTEX,{"disambiguationData":[OD(0.0)],"derivedFrom":[subQ1,subQ0]});Q63=makeQuery(id+"F3.imprint","IMPRINT",FACE,{"disambiguationData":[TD([[makeQuery(id+"F3.imprint","IMPRINT",EDGE,{"disambiguationData":[TD([[subQ2,-1.0]])],"derivedFrom":subQ1}),-1.0]])]});}
            var Q64;
            {var subQ0=sQuery(id+"F3.wireOp",EDGE,"E28");var subQ1=sQuery(id+"F3.wireOp",EDGE,"E27");var subQ2=makeQuery(id+"F3.imprint","INTERSECT",VERTEX,{"disambiguationData":[OD(0.0)],"derivedFrom":[subQ1,subQ0]});Q64=makeQuery(id+"F3.imprint","IMPRINT",FACE,{"disambiguationData":[TD([[makeQuery(id+"F3.imprint","IMPRINT",EDGE,{"disambiguationData":[TD([[subQ2,-1.0]])],"derivedFrom":subQ1}),1.0]])]});}
            var Q65;
            {var subQ0=sQuery(id+"F3.wireOp",EDGE,"E28");var subQ1=sQuery(id+"F3.wireOp",EDGE,"E7");var subQ2=makeQuery(id+"F3.imprint","INTERSECT",VERTEX,{"disambiguationData":[OD(1.0)],"derivedFrom":[subQ1,subQ0]});Q65=makeQuery(id+"F3.imprint","IMPRINT",FACE,{"disambiguationData":[TD([[makeQuery(id+"F3.imprint","IMPRINT",EDGE,{"disambiguationData":[TD([[subQ2,-1.0]])],"derivedFrom":subQ1}),-1.0]])]});}
            var Q66;
            {var subQ0=sQuery(id+"F3.wireOp",EDGE,"E28");var subQ1=sQuery(id+"F3.wireOp",EDGE,"E6");var subQ2=makeQuery(id+"F3.imprint","INTERSECT",VERTEX,{"disambiguationData":[OD(0.0)],"derivedFrom":[subQ1,subQ0]});Q66=makeQuery(id+"F3.imprint","IMPRINT",FACE,{"disambiguationData":[TD([[makeQuery(id+"F3.imprint","IMPRINT",EDGE,{"disambiguationData":[TD([[subQ2,-1.0]])],"derivedFrom":subQ1}),-1.0]])]});}
            var Q67;
            {var subQ0=sQuery(id+"F3.wireOp",EDGE,"E7");var subQ1=sQuery(id+"F3.wireOp",EDGE,"E6");var subQ2=makeQuery(id+"F3.imprint","INTERSECT",VERTEX,{"disambiguationData":[OD(1.0)],"derivedFrom":[subQ1,subQ0]});Q67=makeQuery(id+"F3.imprint","IMPRINT",FACE,{"disambiguationData":[TD([[makeQuery(id+"F3.imprint","IMPRINT",EDGE,{"disambiguationData":[TD([[subQ2,-1.0]])],"derivedFrom":subQ1}),1.0]])]});}
            var Q68;
            {var subQ0=sQuery(id+"F3.wireOp",EDGE,"E28");var subQ1=sQuery(id+"F3.wireOp",EDGE,"E6");var subQ2=makeQuery(id+"F3.imprint","INTERSECT",VERTEX,{"disambiguationData":[OD(0.0)],"derivedFrom":[subQ1,subQ0]});Q68=makeQuery(id+"F3.imprint","IMPRINT",FACE,{"disambiguationData":[TD([[makeQuery(id+"F3.imprint","IMPRINT",EDGE,{"disambiguationData":[TD([[subQ2,-1.0]])],"derivedFrom":subQ1}),1.0]])]});}
            var Q69;
            {var subQ0=sQuery(id+"F3.wireOp",EDGE,"E7");var subQ1=sQuery(id+"F3.wireOp",EDGE,"E6");var subQ2=makeQuery(id+"F3.imprint","INTERSECT",VERTEX,{"disambiguationData":[OD(0.0)],"derivedFrom":[subQ1,subQ0]});Q69=makeQuery(id+"F3.imprint","IMPRINT",FACE,{"disambiguationData":[TD([[makeQuery(id+"F3.imprint","IMPRINT",EDGE,{"disambiguationData":[TD([[subQ2,-1.0]])],"derivedFrom":subQ1}),-1.0]])]});}
            var Q70;
            {var subQ1=sQuery(id+"F3.wireOp",EDGE,"E6");var subQ5=sQuery(id+"F3.wireOp",EDGE,"E5");var subQ6=makeQuery(id+"F3.imprint","INTERSECT",VERTEX,{"disambiguationData":[OD(0.0)],"derivedFrom":[subQ5,subQ1]});Q70=makeQuery(id+"F3.imprint","IMPRINT",FACE,{"disambiguationData":[TD([[makeQuery(id+"F3.imprint","IMPRINT",EDGE,{"disambiguationData":[TD([[subQ6,-1.0]])],"derivedFrom":subQ5}),-1.0]])]});}
            var Q71;
            {var subQ0=sQuery(id+"F3.wireOp",EDGE,"E7");var subQ1=sQuery(id+"F3.wireOp",EDGE,"E6");var subQ2=makeQuery(id+"F3.imprint","INTERSECT",VERTEX,{"disambiguationData":[OD(1.0)],"derivedFrom":[subQ1,subQ0]});Q71=makeQuery(id+"F3.imprint","IMPRINT",FACE,{"disambiguationData":[TD([[makeQuery(id+"F3.imprint","IMPRINT",EDGE,{"disambiguationData":[TD([[subQ2,-1.0]])],"derivedFrom":subQ1}),-1.0]])]});}
            var Q72;
            {var subQ0=sQuery(id+"F3.wireOp",EDGE,"E7");var subQ1=sQuery(id+"F3.wireOp",EDGE,"E6");var subQ2=makeQuery(id+"F3.imprint","INTERSECT",VERTEX,{"disambiguationData":[OD(0.0)],"derivedFrom":[subQ1,subQ0]});Q72=makeQuery(id+"F3.imprint","IMPRINT",FACE,{"disambiguationData":[TD([[makeQuery(id+"F3.imprint","IMPRINT",EDGE,{"disambiguationData":[TD([[subQ2,-1.0]])],"derivedFrom":subQ1}),1.0]])]});}
            var Q73;
            {var subQ0=sQuery(id+"F3.wireOp",EDGE,"E6");var subQ1=sQuery(id+"F3.wireOp",EDGE,"E5");var subQ2=makeQuery(id+"F3.imprint","INTERSECT",VERTEX,{"disambiguationData":[OD(0.0)],"derivedFrom":[subQ1,subQ0]});Q73=makeQuery(id+"F3.imprint","IMPRINT",FACE,{"disambiguationData":[TD([[makeQuery(id+"F3.imprint","IMPRINT",EDGE,{"disambiguationData":[TD([[subQ2,-1.0]])],"derivedFrom":subQ1}),1.0]])]});}
            var Q74;
            {var subQ0=sQuery(id+"F3.wireOp",EDGE,"E8");var subQ1=sQuery(id+"F3.wireOp",EDGE,"E5");var subQ2=makeQuery(id+"F3.imprint","INTERSECT",VERTEX,{"disambiguationData":[OD(1.0)],"derivedFrom":[subQ1,subQ0]});Q74=makeQuery(id+"F3.imprint","IMPRINT",FACE,{"disambiguationData":[TD([[makeQuery(id+"F3.imprint","IMPRINT",EDGE,{"disambiguationData":[TD([[subQ2,-1.0]])],"derivedFrom":subQ1}),-1.0]])]});}
            var Q75;
            {var subQ0=sQuery(id+"F3.wireOp",EDGE,"E8");var subQ1=sQuery(id+"F3.wireOp",EDGE,"E5");var subQ2=makeQuery(id+"F3.imprint","INTERSECT",VERTEX,{"disambiguationData":[OD(1.0)],"derivedFrom":[subQ1,subQ0]});Q75=makeQuery(id+"F3.imprint","IMPRINT",FACE,{"disambiguationData":[TD([[makeQuery(id+"F3.imprint","IMPRINT",EDGE,{"disambiguationData":[TD([[subQ2,-1.0]])],"derivedFrom":subQ1}),1.0]])]});}
            var Q76;
            {var subQ17=sQuery(id+"F3.wireOp",EDGE,"E12");var subQ18=sQuery(id+"F3.wireOp",EDGE,"E11");var subQ19=makeQuery(id+"F3.imprint","INTERSECT",VERTEX,{"disambiguationData":[OD(1.0)],"derivedFrom":[subQ18,subQ17]});Q76=makeQuery(id+"F3.imprint","IMPRINT",FACE,{"disambiguationData":[TD([[makeQuery(id+"F3.imprint","IMPRINT",EDGE,{"disambiguationData":[TD([[subQ19,1.0]])],"derivedFrom":subQ18}),-1.0]])]});}
            var Q77;
            {var subQ0=sQuery(id+"F3.wireOp",EDGE,"E12");var subQ1=sQuery(id+"F3.wireOp",EDGE,"E11");var subQ2=makeQuery(id+"F3.imprint","INTERSECT",VERTEX,{"disambiguationData":[OD(1.0)],"derivedFrom":[subQ1,subQ0]});Q77=makeQuery(id+"F3.imprint","IMPRINT",FACE,{"disambiguationData":[TD([[makeQuery(id+"F3.imprint","IMPRINT",EDGE,{"disambiguationData":[TD([[subQ2,-1.0]])],"derivedFrom":subQ1}),-1.0]])]});}
            var Q78;
            {var subQ0=sQuery(id+"F3.wireOp",EDGE,"E13");var subQ1=sQuery(id+"F3.wireOp",EDGE,"E12");var subQ2=makeQuery(id+"F3.imprint","INTERSECT",VERTEX,{"disambiguationData":[OD(1.0)],"derivedFrom":[subQ1,subQ0]});Q78=makeQuery(id+"F3.imprint","IMPRINT",FACE,{"disambiguationData":[TD([[makeQuery(id+"F3.imprint","IMPRINT",EDGE,{"disambiguationData":[TD([[subQ2,-1.0]])],"derivedFrom":subQ1}),1.0]])]});}
            var Q79;
            {var subQ0=sQuery(id+"F3.wireOp",EDGE,"E13");var subQ1=sQuery(id+"F3.wireOp",EDGE,"E12");var subQ2=makeQuery(id+"F3.imprint","INTERSECT",VERTEX,{"disambiguationData":[OD(1.0)],"derivedFrom":[subQ1,subQ0]});Q79=makeQuery(id+"F3.imprint","IMPRINT",FACE,{"disambiguationData":[TD([[makeQuery(id+"F3.imprint","IMPRINT",EDGE,{"disambiguationData":[TD([[subQ2,-1.0]])],"derivedFrom":subQ1}),-1.0]])]});}
            var Q80;
            {var subQ0=sQuery(id+"F3.wireOp",EDGE,"E12");var subQ1=sQuery(id+"F3.wireOp",EDGE,"E11");var subQ2=makeQuery(id+"F3.imprint","INTERSECT",VERTEX,{"disambiguationData":[OD(1.0)],"derivedFrom":[subQ1,subQ0]});Q80=makeQuery(id+"F3.imprint","IMPRINT",FACE,{"disambiguationData":[TD([[makeQuery(id+"F3.imprint","IMPRINT",EDGE,{"disambiguationData":[TD([[subQ2,1.0]])],"derivedFrom":subQ1}),1.0]])]});}
            var Q81;
            {var subQ0=sQuery(id+"F3.wireOp",EDGE,"E12");var subQ1=sQuery(id+"F3.wireOp",EDGE,"E11");var subQ2=makeQuery(id+"F3.imprint","INTERSECT",VERTEX,{"disambiguationData":[OD(1.0)],"derivedFrom":[subQ1,subQ0]});Q81=makeQuery(id+"F3.imprint","IMPRINT",FACE,{"disambiguationData":[TD([[makeQuery(id+"F3.imprint","IMPRINT",EDGE,{"disambiguationData":[TD([[subQ2,-1.0]])],"derivedFrom":subQ1}),1.0]])]});}
            var Q82;
            {var subQ0=sQuery(id+"F3.wireOp",EDGE,"E26");var subQ1=sQuery(id+"F3.wireOp",EDGE,"E24");var subQ2=makeQuery(id+"F3.imprint","INTERSECT",VERTEX,{"derivedFrom":[subQ1,subQ0]});Q82=makeQuery(id+"F3.imprint","IMPRINT",FACE,{"disambiguationData":[TD([[makeQuery(id+"F3.imprint","IMPRINT",EDGE,{"disambiguationData":[TD([[subQ2,-1.0]])],"derivedFrom":subQ1}),-1.0]])]});}
            var Q83;
            {var subQ0=sQuery(id+"F3.wireOp",EDGE,"E17");var subQ1=makeQuery(id+"F1.opExtrude","CAP_EDGE",EDGE,{"disambiguationData":[OSD([sQuery(id+"F0.wireOp",EDGE,"E0")])],"isStart":false});var subQ2=makeQuery(id+"F3.imprint","INTERSECT",VERTEX,{"disambiguationData":[OD(0.0)],"derivedFrom":[subQ1,subQ0]});Q83=makeQuery(id+"F3.imprint","IMPRINT",FACE,{"disambiguationData":[TD([[makeQuery(id+"F3.imprint","IMPRINT",EDGE,{"disambiguationData":[TD([[subQ2,-1.0]])],"derivedFrom":subQ0}),1.0]])]});}
            var Q84;
            {var subQ0=sQuery(id+"F3.wireOp",EDGE,"E21");var subQ1=sQuery(id+"F3.wireOp",EDGE,"E19");var subQ2=makeQuery(id+"F3.imprint","INTERSECT",VERTEX,{"derivedFrom":[subQ1,subQ0]});Q84=makeQuery(id+"F3.imprint","IMPRINT",FACE,{"disambiguationData":[TD([[makeQuery(id+"F3.imprint","IMPRINT",EDGE,{"disambiguationData":[TD([[subQ2,1.0]])],"derivedFrom":subQ1}),-1.0]])]});}
            var Q85;
            {var subQ0=sQuery(id+"F3.wireOp",EDGE,"E17");var subQ1=sQuery(id+"F3.wireOp",EDGE,"E13");var subQ2=makeQuery(id+"F3.imprint","INTERSECT",VERTEX,{"disambiguationData":[OD(1.0)],"derivedFrom":[subQ1,subQ0]});Q85=makeQuery(id+"F3.imprint","IMPRINT",FACE,{"disambiguationData":[TD([[makeQuery(id+"F3.imprint","IMPRINT",EDGE,{"disambiguationData":[TD([[subQ2,1.0]])],"derivedFrom":subQ1}),-1.0]])]});}
            var Q86;
            {var subQ0=sQuery(id+"F3.wireOp",EDGE,"E28");var subQ1=sQuery(id+"F3.wireOp",EDGE,"E7");var subQ2=makeQuery(id+"F3.imprint","INTERSECT",VERTEX,{"disambiguationData":[OD(1.0)],"derivedFrom":[subQ1,subQ0]});Q86=makeQuery(id+"F3.imprint","IMPRINT",FACE,{"disambiguationData":[TD([[makeQuery(id+"F3.imprint","IMPRINT",EDGE,{"disambiguationData":[TD([[subQ2,-1.0]])],"derivedFrom":subQ1}),1.0]])]});}
            var Q87;
            {var subQ0=sQuery(id+"F3.wireOp",EDGE,"E28");var subQ1=sQuery(id+"F3.wireOp",EDGE,"E7");var subQ2=makeQuery(id+"F3.imprint","INTERSECT",VERTEX,{"disambiguationData":[OD(1.0)],"derivedFrom":[subQ1,subQ0]});Q87=makeQuery(id+"F3.imprint","IMPRINT",FACE,{"disambiguationData":[TD([[makeQuery(id+"F3.imprint","IMPRINT",EDGE,{"disambiguationData":[TD([[subQ2,1.0]])],"derivedFrom":subQ1}),1.0]])]});}
            var Q88;
            {var subQ0=sQuery(id+"F0.wireOp",EDGE,"E3");var subQ1=sQuery(id+"F0.wireOp",EDGE,"E2");var subQ2=sQuery(id+"F0.wireOp",EDGE,"E1");var subQ3=sQuery(id+"F0.wireOp",EDGE,"E0");Q88=makeQuery(id+"F2.boolean.opBoolean","MERGE",FACE,{"derivedFrom":[makeQuery(id+"F1.opExtrude","CAP_FACE",FACE,{"disambiguationData":[OSD([subQ3,subQ2,subQ1,subQ0])],"isStart":true}),makeQuery(id+"F2.opExtrude","CAP_FACE",FACE,{"disambiguationData":[OSD([subQ3,subQ2,subQ1,subQ0])],"isStart":true})]});}
            extrude(context, id + "F4", {"entities" : qUnion([Q0, Q1, Q2, Q3, Q4, Q5, Q6, Q7, Q8, Q9, Q10, Q11, Q12, Q13, Q14, Q15, Q16, Q17, Q18, Q19, Q20, Q21, Q22, Q23, Q24, Q25, Q26, Q27, Q28, Q29, Q30, Q31, Q32, Q33, Q34, Q35, Q36, Q37, Q38, Q39, Q40, Q41, Q42, Q43, Q44, Q45, Q46, Q47, Q48, Q49, Q50, Q51, Q52, Q53, Q54, Q55, Q56, Q57, Q58, Q59, Q60, Q61, Q62, Q63, Q64, Q65, Q66, Q67, Q68, Q69, Q70, Q71, Q72, Q73, Q74, Q75, Q76, Q77, Q78, Q79, Q80, Q81, Q82, Q83, Q84, Q85, Q86, Q87]), "endBound" : BoundingType.UP_TO_SURFACE, "oppositeDirection" : true, "endBoundEntityFace" : qUnion([Q88]), "depth" : 25.4 * mm, "hasSecondDirection" : true, "secondDirectionOppositeDirection" : false, "secondDirectionDepth" : 1.27 * mm});
        }
        {
            var Q0;
            Q0=makeQuery(id+"F1.opExtrude","CAP_FACE",FACE,{"disambiguationData":[OSD([sQuery(id+"F0.wireOp",EDGE,"E0"),sQuery(id+"F0.wireOp",EDGE,"E1"),sQuery(id+"F0.wireOp",EDGE,"E2"),sQuery(id+"F0.wireOp",EDGE,"E3")])],"isStart":false});
            var sketch = newSketch(context, id + "F5", { "sketchPlane" : qUnion([Q0])});
            skFitSpline(sketch, "E29", {"points": [v(-15.94, 31.35) * mm, v(19.55, 57.69) * mm, v(15.38, 31.51) * mm], "startDerivative": vector(55.56, 201.3) * mm, "endDerivative": vector(33.74, -137) * mm});
            skLineSegment(sketch, "E30", {"start": v(-15.94, 31.35) * mm, "end": v(-15.7, 28.72) * mm});
            skLineSegment(sketch, "E31", {"start": v(-15.7, 28.72) * mm, "end": v(16.33, 28.72) * mm});
            skLineSegment(sketch, "E32", {"start": v(16.33, 28.72) * mm, "end": v(15.38, 31.35) * mm});
            skLineSegment(sketch, "E33", {"start": v(15.38, 31.35) * mm, "end": v(15.38, 31.51) * mm});
            skSolve(sketch);
        }
        {
            var Q0;
            Q0=makeQuery(id+"F5.imprint","IMPRINT",FACE,{"disambiguationData":[TD([[makeQuery(id+"F5.imprint","IMPRINT",EDGE,{"derivedFrom":sQuery(id+"F5.wireOp",EDGE,"E29")}),-1.0]])]});
            var Q1;
            {var subQ0=sQuery(id+"F0.wireOp",EDGE,"E3");var subQ1=sQuery(id+"F0.wireOp",EDGE,"E2");var subQ2=sQuery(id+"F0.wireOp",EDGE,"E1");var subQ3=sQuery(id+"F0.wireOp",EDGE,"E0");Q1=makeQuery(id+"F2.boolean.opBoolean","MERGE",FACE,{"derivedFrom":[makeQuery(id+"F1.opExtrude","CAP_FACE",FACE,{"disambiguationData":[OSD([subQ3,subQ2,subQ1,subQ0])],"isStart":true}),makeQuery(id+"F2.opExtrude","CAP_FACE",FACE,{"disambiguationData":[OSD([subQ3,subQ2,subQ1,subQ0])],"isStart":true})]});}
            extrude(context, id + "F6", {"entities" : qUnion([Q0]), "operationType" : NewBodyOperationType.ADD, "endBound" : BoundingType.UP_TO_SURFACE, "oppositeDirection" : true, "endBoundEntityFace" : qUnion([Q1]), "depth" : 25.4 * mm});
        }
        {
            var Q0;
            Q0=makeQuery(id+"F4.opExtrude","CAP_FACE",FACE,{"disambiguationData":[OSD([sQuery(id+"F3.wireOp",EDGE,"E5"),sQuery(id+"F3.wireOp",EDGE,"E6"),sQuery(id+"F3.wireOp",EDGE,"E7"),sQuery(id+"F3.wireOp",EDGE,"E8"),sQuery(id+"F3.wireOp",EDGE,"E9"),sQuery(id+"F3.wireOp",EDGE,"E10"),sQuery(id+"F3.wireOp",EDGE,"E11"),sQuery(id+"F3.wireOp",EDGE,"E12"),sQuery(id+"F3.wireOp",EDGE,"E13"),sQuery(id+"F3.wireOp",EDGE,"E14"),sQuery(id+"F3.wireOp",EDGE,"E15"),sQuery(id+"F3.wireOp",EDGE,"E16"),sQuery(id+"F3.wireOp",EDGE,"E17"),sQuery(id+"F3.wireOp",EDGE,"E18"),sQuery(id+"F3.wireOp",EDGE,"E19"),sQuery(id+"F3.wireOp",EDGE,"E20"),sQuery(id+"F3.wireOp",EDGE,"E21"),sQuery(id+"F3.wireOp",EDGE,"E22"),sQuery(id+"F3.wireOp",EDGE,"E23"),sQuery(id+"F3.wireOp",EDGE,"E24"),sQuery(id+"F3.wireOp",EDGE,"E25"),sQuery(id+"F3.wireOp",EDGE,"E26"),sQuery(id+"F3.wireOp",EDGE,"E27"),sQuery(id+"F3.wireOp",EDGE,"E28")])],"isStart":true});
            var sketch = newSketch(context, id + "F7", { "sketchPlane" : qUnion([Q0])});
            skCircle(sketch, "E34", {"center": v(19.67, 58.85) * mm, "radius": 2.03 * mm});
            skCircle(sketch, "E35", {"center": v(17.64, 58.7) * mm, "radius": 2.03 * mm});
            skCircle(sketch, "E36", {"center": v(17.56, 56.67) * mm, "radius": 2.03 * mm});
            skCircle(sketch, "E37", {"center": v(19.6, 56.82) * mm, "radius": 2.03 * mm});
            skSolve(sketch);
        }
        {
            var Q0;
            {var subQ0=sQuery(id+"F7.wireOp",EDGE,"E35");var subQ1=sQuery(id+"F7.wireOp",EDGE,"E34");var subQ2=makeQuery(id+"F7.imprint","INTERSECT",VERTEX,{"disambiguationData":[OD(0.0)],"derivedFrom":[subQ1,subQ0]});Q0=makeQuery(id+"F7.imprint","IMPRINT",FACE,{"disambiguationData":[TD([[makeQuery(id+"F7.imprint","IMPRINT",EDGE,{"disambiguationData":[TD([[subQ2,-1.0]])],"derivedFrom":subQ1}),-1.0]])]});}
            var Q1;
            {var subQ0=sQuery(id+"F7.wireOp",EDGE,"E36");var subQ1=sQuery(id+"F7.wireOp",EDGE,"E35");var subQ2=makeQuery(id+"F7.imprint","INTERSECT",VERTEX,{"disambiguationData":[OD(0.0)],"derivedFrom":[subQ1,subQ0]});Q1=makeQuery(id+"F7.imprint","IMPRINT",FACE,{"disambiguationData":[TD([[makeQuery(id+"F7.imprint","IMPRINT",EDGE,{"disambiguationData":[TD([[subQ2,-1.0]])],"derivedFrom":subQ1}),-1.0]])]});}
            var Q2;
            {var subQ0=sQuery(id+"F7.wireOp",EDGE,"E35");var subQ1=sQuery(id+"F7.wireOp",EDGE,"E34");var subQ2=makeQuery(id+"F7.imprint","INTERSECT",VERTEX,{"disambiguationData":[OD(1.0)],"derivedFrom":[subQ1,subQ0]});Q2=makeQuery(id+"F7.imprint","IMPRINT",FACE,{"disambiguationData":[TD([[makeQuery(id+"F7.imprint","IMPRINT",EDGE,{"disambiguationData":[TD([[subQ2,-1.0]])],"derivedFrom":subQ1}),-1.0]])]});}
            var Q3;
            {var subQ0=sQuery(id+"F7.wireOp",EDGE,"E37");var subQ1=sQuery(id+"F7.wireOp",EDGE,"E34");var subQ2=makeQuery(id+"F7.imprint","INTERSECT",VERTEX,{"disambiguationData":[OD(1.0)],"derivedFrom":[subQ1,subQ0]});Q3=makeQuery(id+"F7.imprint","IMPRINT",FACE,{"disambiguationData":[TD([[makeQuery(id+"F7.imprint","IMPRINT",EDGE,{"disambiguationData":[TD([[subQ2,-1.0]])],"derivedFrom":subQ1}),-1.0]])]});}
            var Q4;
            {var subQ0=sQuery(id+"F7.wireOp",EDGE,"E36");var subQ1=sQuery(id+"F7.wireOp",EDGE,"E34");var subQ2=makeQuery(id+"F7.imprint","INTERSECT",VERTEX,{"disambiguationData":[OD(0.0)],"derivedFrom":[subQ1,subQ0]});Q4=makeQuery(id+"F7.imprint","IMPRINT",FACE,{"disambiguationData":[TD([[makeQuery(id+"F7.imprint","IMPRINT",EDGE,{"disambiguationData":[TD([[subQ2,-1.0]])],"derivedFrom":subQ1}),-1.0]])]});}
            var Q5;
            {var subQ0=sQuery(id+"F7.wireOp",EDGE,"E36");var subQ1=sQuery(id+"F7.wireOp",EDGE,"E34");var subQ2=makeQuery(id+"F7.imprint","INTERSECT",VERTEX,{"disambiguationData":[OD(0.0)],"derivedFrom":[subQ1,subQ0]});Q5=makeQuery(id+"F7.imprint","IMPRINT",FACE,{"disambiguationData":[TD([[makeQuery(id+"F7.imprint","IMPRINT",EDGE,{"disambiguationData":[TD([[subQ2,-1.0]])],"derivedFrom":subQ1}),1.0]])]});}
            var Q6;
            {var subQ0=sQuery(id+"F7.wireOp",EDGE,"E35");var subQ1=sQuery(id+"F7.wireOp",EDGE,"E34");var subQ2=makeQuery(id+"F7.imprint","INTERSECT",VERTEX,{"disambiguationData":[OD(0.0)],"derivedFrom":[subQ1,subQ0]});Q6=makeQuery(id+"F7.imprint","IMPRINT",FACE,{"disambiguationData":[TD([[makeQuery(id+"F7.imprint","IMPRINT",EDGE,{"disambiguationData":[TD([[subQ2,-1.0]])],"derivedFrom":subQ1}),1.0]])]});}
            var Q7;
            {var subQ0=sQuery(id+"F7.wireOp",EDGE,"E37");var subQ1=sQuery(id+"F7.wireOp",EDGE,"E35");var subQ2=makeQuery(id+"F7.imprint","INTERSECT",VERTEX,{"disambiguationData":[OD(0.0)],"derivedFrom":[subQ1,subQ0]});Q7=makeQuery(id+"F7.imprint","IMPRINT",FACE,{"disambiguationData":[TD([[makeQuery(id+"F7.imprint","IMPRINT",EDGE,{"disambiguationData":[TD([[subQ2,1.0]])],"derivedFrom":subQ1}),1.0]])]});}
            var Q8;
            {var subQ0=sQuery(id+"F7.wireOp",EDGE,"E37");var subQ1=sQuery(id+"F7.wireOp",EDGE,"E34");var subQ2=makeQuery(id+"F7.imprint","INTERSECT",VERTEX,{"disambiguationData":[OD(1.0)],"derivedFrom":[subQ1,subQ0]});Q8=makeQuery(id+"F7.imprint","IMPRINT",FACE,{"disambiguationData":[TD([[makeQuery(id+"F7.imprint","IMPRINT",EDGE,{"disambiguationData":[TD([[subQ2,-1.0]])],"derivedFrom":subQ1}),1.0]])]});}
            var Q9;
            {var subQ0=sQuery(id+"F7.wireOp",EDGE,"E35");var subQ1=sQuery(id+"F7.wireOp",EDGE,"E34");var subQ2=makeQuery(id+"F7.imprint","INTERSECT",VERTEX,{"disambiguationData":[OD(1.0)],"derivedFrom":[subQ1,subQ0]});Q9=makeQuery(id+"F7.imprint","IMPRINT",FACE,{"disambiguationData":[TD([[makeQuery(id+"F7.imprint","IMPRINT",EDGE,{"disambiguationData":[TD([[subQ2,-1.0]])],"derivedFrom":subQ1}),1.0]])]});}
            var Q10;
            {var subQ0=sQuery(id+"F7.wireOp",EDGE,"E37");var subQ1=sQuery(id+"F7.wireOp",EDGE,"E34");var subQ2=makeQuery(id+"F7.imprint","INTERSECT",VERTEX,{"disambiguationData":[OD(0.0)],"derivedFrom":[subQ1,subQ0]});Q10=makeQuery(id+"F7.imprint","IMPRINT",FACE,{"disambiguationData":[TD([[makeQuery(id+"F7.imprint","IMPRINT",EDGE,{"disambiguationData":[TD([[subQ2,1.0]])],"derivedFrom":subQ1}),1.0]])]});}
            var Q11;
            {var subQ0=sQuery(id+"F7.wireOp",EDGE,"E37");var subQ1=sQuery(id+"F7.wireOp",EDGE,"E34");var subQ2=makeQuery(id+"F7.imprint","INTERSECT",VERTEX,{"disambiguationData":[OD(0.0)],"derivedFrom":[subQ1,subQ0]});Q11=makeQuery(id+"F7.imprint","IMPRINT",FACE,{"disambiguationData":[TD([[makeQuery(id+"F7.imprint","IMPRINT",EDGE,{"disambiguationData":[TD([[subQ2,1.0]])],"derivedFrom":subQ1}),-1.0]])]});}
            var Q12;
            {var subQ0=sQuery(id+"F7.wireOp",EDGE,"E35");var subQ1=sQuery(id+"F7.wireOp",EDGE,"E34");var subQ2=makeQuery(id+"F7.imprint","INTERSECT",VERTEX,{"disambiguationData":[OD(0.0)],"derivedFrom":[subQ1,subQ0]});Q12=makeQuery(id+"F7.imprint","IMPRINT",FACE,{"disambiguationData":[TD([[makeQuery(id+"F7.imprint","IMPRINT",EDGE,{"disambiguationData":[TD([[subQ2,1.0]])],"derivedFrom":subQ1}),1.0]])]});}
            var Q13;
            {var subQ0=sQuery(id+"F0.wireOp",EDGE,"E3");var subQ1=sQuery(id+"F0.wireOp",EDGE,"E2");var subQ2=sQuery(id+"F0.wireOp",EDGE,"E1");var subQ3=sQuery(id+"F0.wireOp",EDGE,"E0");Q13=makeQuery(id+"F2.boolean.opBoolean","MERGE",FACE,{"derivedFrom":[makeQuery(id+"F1.opExtrude","CAP_FACE",FACE,{"disambiguationData":[OSD([subQ3,subQ2,subQ1,subQ0])],"isStart":true}),makeQuery(id+"F2.opExtrude","CAP_FACE",FACE,{"disambiguationData":[OSD([subQ3,subQ2,subQ1,subQ0])],"isStart":true})]});}
            extrude(context, id + "F8", {"entities" : qUnion([Q0, Q1, Q2, Q3, Q4, Q5, Q6, Q7, Q8, Q9, Q10, Q11, Q12]), "operationType" : NewBodyOperationType.ADD, "endBound" : BoundingType.UP_TO_SURFACE, "oppositeDirection" : true, "endBoundEntityFace" : qUnion([Q13]), "depth" : 25.4 * mm});
        }
        {
            var Q0;
            Q0=makeQuery(id+"F1.opExtrude","CAP_FACE",FACE,{"disambiguationData":[OSD([sQuery(id+"F0.wireOp",EDGE,"E0"),sQuery(id+"F0.wireOp",EDGE,"E1"),sQuery(id+"F0.wireOp",EDGE,"E2"),sQuery(id+"F0.wireOp",EDGE,"E3")])],"isStart":false});
            var sketch = newSketch(context, id + "F9", { "sketchPlane" : qUnion([Q0])});
            skEllipse(sketch, "E38", {"center": v(-8.45, 7.96) * mm, "majorRadius": 3.81 * mm, "minorRadius": 2.54 * mm, "majorAxis": v(0, 1)});
            skLineSegment(sketch, "E39", {"start": v(0, 17.65) * mm, "end": v(0, 4.33) * mm, "construction": true});
            skEllipse(sketch, "E40.MirrorC", {"center": v(8.45, 7.96) * mm, "majorRadius": 3.81 * mm, "minorRadius": 2.54 * mm, "majorAxis": v(0, 1)});
            skSolve(sketch);
        }
        {
            var Q0;
            Q0 = qSketchRegion(id + "F9", true);
            extrude(context, id + "F10", {"entities" : qUnion([Q0]), "operationType" : NewBodyOperationType.ADD, "depth" : 1.27 * mm});
        }
    });
